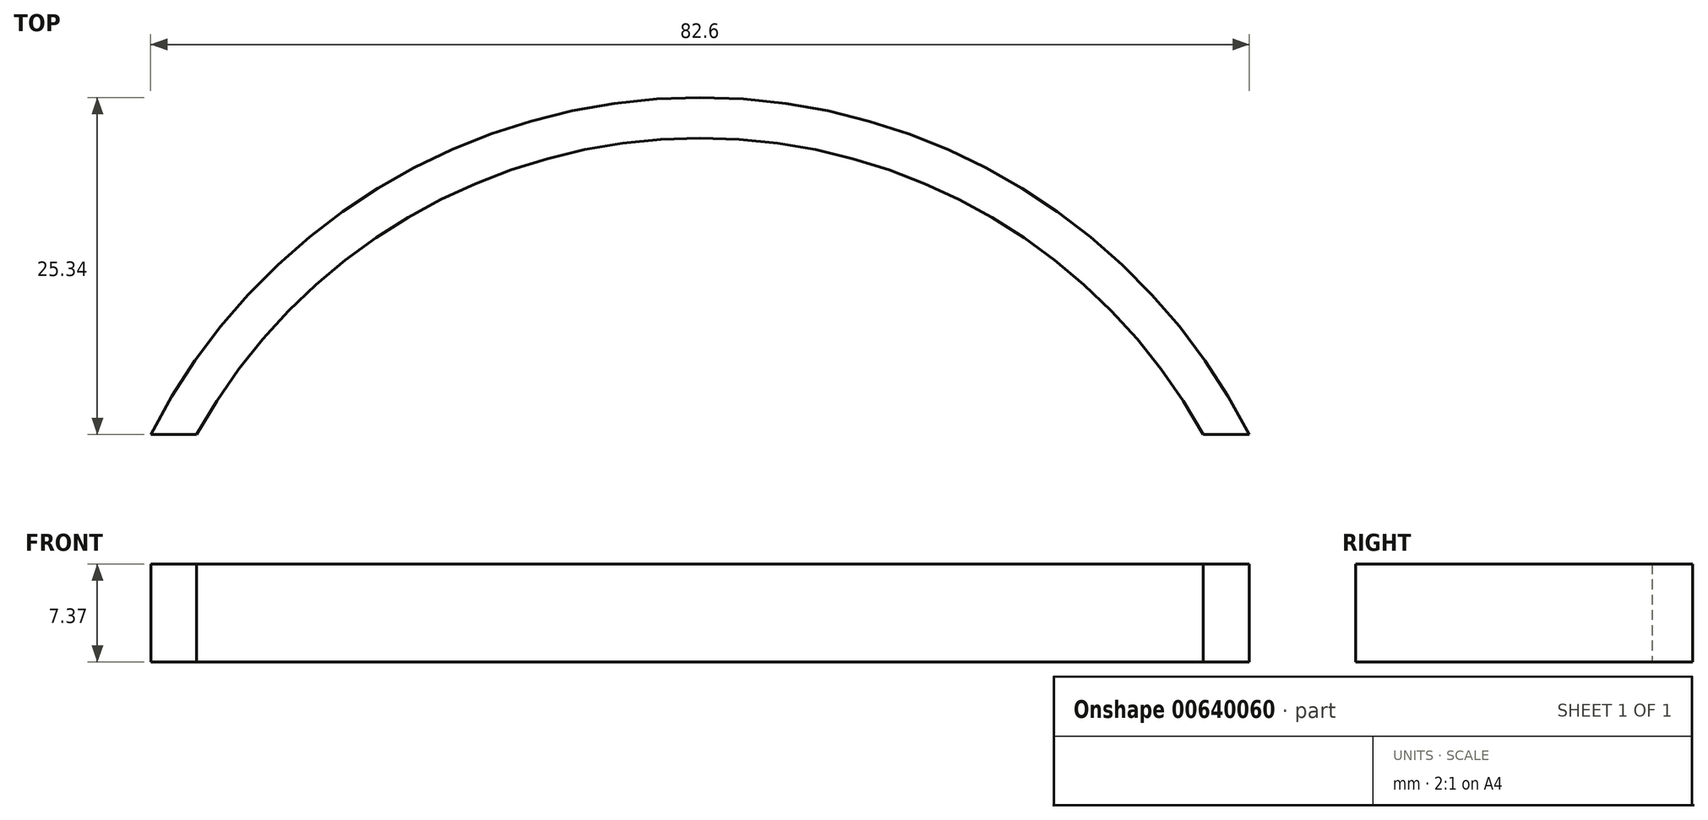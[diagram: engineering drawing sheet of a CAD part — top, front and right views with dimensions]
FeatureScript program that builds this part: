
annotation { "Feature Type Name" : "Feature", "Feature Type Description" : "" }
export const myFeature = defineFeature(function(context is Context, id is Id, definition is map)
    precondition{}
    {
        {
            var Q0;
            Q0=qCreatedBy(makeId("Top.planeOp"),FACE);
            var sketch = newSketch(context, id + "F0", { "sketchPlane" : qUnion([Q0])});
            skArc(sketch, "E0", {"start": v(16.77, 0) * mm, "mid": v(-21.08, 22.3) * mm, "end": v(-58.93, 0) * mm});
            skArc(sketch, "E1.0", {"start": v(20.22, 0) * mm, "mid": v(-21.08, 25.34) * mm, "end": v(-62.38, 0) * mm});
            skLineSegment(sketch, "E2", {"start": v(-62.38, 0) * mm, "end": v(-58.93, 0) * mm});
            skLineSegment(sketch, "E3", {"start": v(20.22, 0) * mm, "end": v(16.77, 0) * mm});
            skLineSegment(sketch, "E4", {"start": v(-62.38, 0) * mm, "end": v(-62.38, 0) * mm});
            skSolve(sketch);
        }
        {
            var Q0;
            {var subQ0=sQuery(id+"F0.wireOp",EDGE,"E2");Q0=makeQuery(id+"F0.imprint","IMPRINT",FACE,{"disambiguationData":[TD([[makeQuery(id+"F0.imprint","IMPRINT",EDGE,{"derivedFrom":subQ0}),1.0]])]});}
            var Q1;
            {var subQ0=sQuery(id+"F0.wireOp",EDGE,"E0");Q1=makeQuery(id+"F0.imprint","IMPRINT",FACE,{"disambiguationData":[TD([[makeQuery(id+"F0.imprint","IMPRINT",EDGE,{"derivedFrom":subQ0}),-1.0]])]});}
            var Q2;
            {var subQ0=sQuery(id+"F0.wireOp",EDGE,"E3");Q2=makeQuery(id+"F0.imprint","IMPRINT",FACE,{"disambiguationData":[TD([[makeQuery(id+"F0.imprint","IMPRINT",EDGE,{"derivedFrom":subQ0}),-1.0]])]});}
            extrude(context, id + "F1", {"entities" : qUnion([Q0, Q1, Q2]), "depth" : 7.37 * mm, "offsetDistance" : 25.4 * mm});
        }
    });
